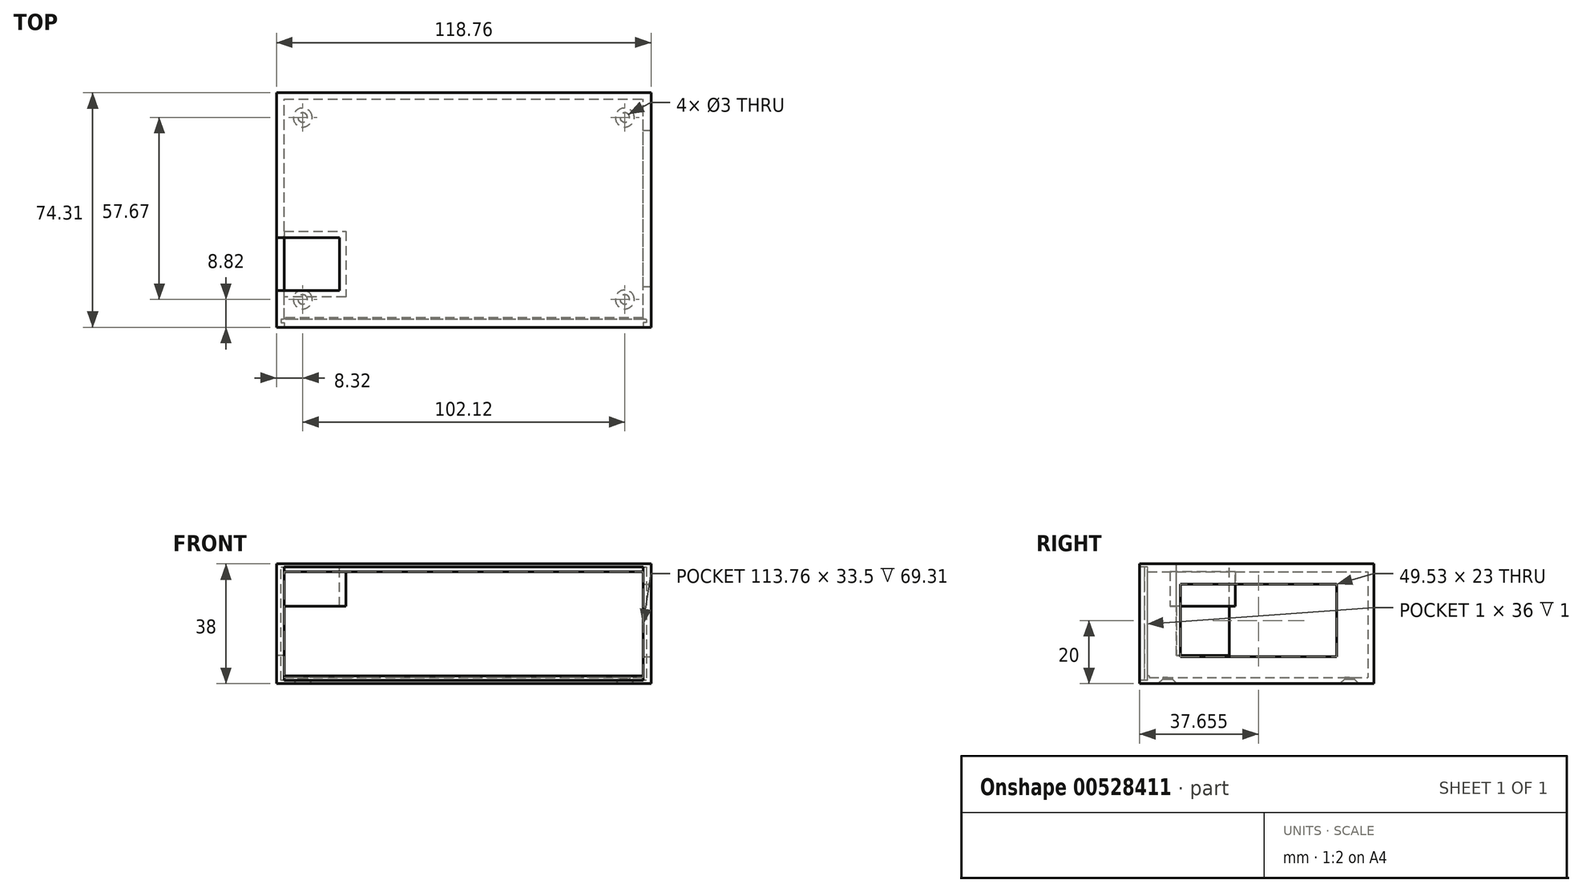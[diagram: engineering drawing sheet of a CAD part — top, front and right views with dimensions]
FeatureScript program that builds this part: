
annotation { "Feature Type Name" : "Feature", "Feature Type Description" : "" }
export const myFeature = defineFeature(function(context is Context, id is Id, definition is map)
    precondition{}
    {
        {
            var Q0;
            Q0=qCreatedBy(makeId("Top.planeOp"),FACE);
            var sketch = newSketch(context, id + "F0", { "sketchPlane" : qUnion([Q0])});
            skLineSegment(sketch, "E0.bottom", {"start": v(0, 0) * mm, "end": v(111.76, 0) * mm, "construction": true});
            skLineSegment(sketch, "E0.top", {"start": v(0, 67.31) * mm, "end": v(111.76, 67.31) * mm, "construction": true});
            skLineSegment(sketch, "E0.left", {"start": v(0, 0) * mm, "end": v(0, 67.3) * mm, "construction": true});
            skLineSegment(sketch, "E0.right", {"start": v(111.76, 0) * mm, "end": v(111.76, 67.3) * mm, "construction": true});
            skLineSegment(sketch, "E1", {"start": v(0, 4.82) * mm, "end": v(4.82, 4.82) * mm, "construction": true});
            skLineSegment(sketch, "E2", {"start": v(4.82, 4.82) * mm, "end": v(4.82, 0) * mm, "construction": true});
            skCircle(sketch, "E3", {"center": v(4.82, 4.82) * mm, "radius": 1.5 * mm});
            skLineSegment(sketch, "E4", {"start": v(0, 33.65) * mm, "end": v(111.76, 33.65) * mm, "construction": true});
            skLineSegment(sketch, "E5", {"start": v(55.88, 67.31) * mm, "end": v(55.88, 0) * mm, "construction": true});
            skCircle(sketch, "E6.MirrorC", {"center": v(4.82, 62.49) * mm, "radius": 1.5 * mm});
            skCircle(sketch, "E7.MirrorC", {"center": v(106.94, 62.5) * mm, "radius": 1.5 * mm});
            skCircle(sketch, "E8.MirrorC", {"center": v(106.94, 4.82) * mm, "radius": 1.5 * mm});
            skLineSegment(sketch, "E9.bottom", {"start": v(-1, -1) * mm, "end": v(112.76, -1) * mm});
            skLineSegment(sketch, "E9.top", {"start": v(-1, 68.31) * mm, "end": v(112.76, 68.31) * mm});
            skLineSegment(sketch, "E9.left", {"start": v(-1, -1) * mm, "end": v(-1, 68.31) * mm});
            skLineSegment(sketch, "E9.right", {"start": v(112.76, -1) * mm, "end": v(112.76, 68.31) * mm});
            skLineSegment(sketch, "E10", {"start": v(0, 0) * mm, "end": v(0, -1) * mm, "construction": true});
            skLineSegment(sketch, "E11", {"start": v(0, 0) * mm, "end": v(-1, 0) * mm, "construction": true});
            skLineSegment(sketch, "E12", {"start": v(0, 67.31) * mm, "end": v(0, 68.31) * mm, "construction": true});
            skLineSegment(sketch, "E13", {"start": v(111.76, 67.31) * mm, "end": v(112.76, 67.31) * mm, "construction": true});
            skLineSegment(sketch, "E14.bottom", {"start": v(-3.5, -4) * mm, "end": v(115.26, -4) * mm});
            skLineSegment(sketch, "E14.top", {"start": v(-3.5, 70.31) * mm, "end": v(115.26, 70.31) * mm});
            skLineSegment(sketch, "E14.left", {"start": v(-3.5, -4) * mm, "end": v(-3.5, 70.31) * mm});
            skLineSegment(sketch, "E14.right", {"start": v(115.26, -4) * mm, "end": v(115.26, 70.31) * mm});
            skLineSegment(sketch, "E15", {"start": v(-1, -1) * mm, "end": v(-1, -4) * mm, "construction": true});
            skLineSegment(sketch, "E16", {"start": v(-1, -1) * mm, "end": v(-3.5, -1) * mm, "construction": true});
            skLineSegment(sketch, "E17", {"start": v(-1, 68.31) * mm, "end": v(-1, 70.31) * mm, "construction": true});
            skLineSegment(sketch, "E18", {"start": v(112.76, 68.31) * mm, "end": v(115.26, 68.31) * mm, "construction": true});
            skCircle(sketch, "E19", {"center": v(4.82, 4.82) * mm, "radius": 3 * mm});
            skCircle(sketch, "E20.MirrorC", {"center": v(4.82, 62.49) * mm, "radius": 3 * mm});
            skCircle(sketch, "E21.MirrorC", {"center": v(106.94, 62.5) * mm, "radius": 3 * mm});
            skCircle(sketch, "E22.MirrorC", {"center": v(106.94, 4.82) * mm, "radius": 3 * mm});
            skSolve(sketch);
        }
        {
            var Q0;
            Q0=makeQuery(id+"F0.imprint","IMPRINT",FACE,{"disambiguationData":[TD([[makeQuery(id+"F0.imprint","IMPRINT",EDGE,{"derivedFrom":sQuery(id+"F0.wireOp",EDGE,"E9.bottom")}),1.0]])]});
            var Q1;
            Q1=makeQuery(id+"F0.imprint","IMPRINT",FACE,{"disambiguationData":[TD([[makeQuery(id+"F0.imprint","IMPRINT",EDGE,{"derivedFrom":sQuery(id+"F0.wireOp",EDGE,"E7.MirrorC")}),-1.0]])]});
            var Q2;
            Q2=makeQuery(id+"F0.imprint","IMPRINT",FACE,{"disambiguationData":[TD([[makeQuery(id+"F0.imprint","IMPRINT",EDGE,{"derivedFrom":sQuery(id+"F0.wireOp",EDGE,"E7.MirrorC")}),1.0]])]});
            var Q3;
            Q3=makeQuery(id+"F0.imprint","IMPRINT",FACE,{"disambiguationData":[TD([[makeQuery(id+"F0.imprint","IMPRINT",EDGE,{"derivedFrom":sQuery(id+"F0.wireOp",EDGE,"E8.MirrorC")}),1.0]])]});
            var Q4;
            Q4=makeQuery(id+"F0.imprint","IMPRINT",FACE,{"disambiguationData":[TD([[makeQuery(id+"F0.imprint","IMPRINT",EDGE,{"derivedFrom":sQuery(id+"F0.wireOp",EDGE,"E8.MirrorC")}),-1.0]])]});
            var Q5;
            Q5=makeQuery(id+"F0.imprint","IMPRINT",FACE,{"disambiguationData":[TD([[makeQuery(id+"F0.imprint","IMPRINT",EDGE,{"derivedFrom":sQuery(id+"F0.wireOp",EDGE,"E3")}),-1.0]])]});
            var Q6;
            Q6=makeQuery(id+"F0.imprint","IMPRINT",FACE,{"disambiguationData":[TD([[makeQuery(id+"F0.imprint","IMPRINT",EDGE,{"derivedFrom":sQuery(id+"F0.wireOp",EDGE,"E3")}),1.0]])]});
            var Q7;
            Q7=makeQuery(id+"F0.imprint","IMPRINT",FACE,{"disambiguationData":[TD([[makeQuery(id+"F0.imprint","IMPRINT",EDGE,{"derivedFrom":sQuery(id+"F0.wireOp",EDGE,"E6.MirrorC")}),1.0]])]});
            var Q8;
            Q8=makeQuery(id+"F0.imprint","IMPRINT",FACE,{"disambiguationData":[TD([[makeQuery(id+"F0.imprint","IMPRINT",EDGE,{"derivedFrom":sQuery(id+"F0.wireOp",EDGE,"E6.MirrorC")}),-1.0]])]});
            extrude(context, id + "F1", {"entities" : qUnion([Q0, Q1, Q2, Q3, Q4, Q5, Q6, Q7, Q8]), "depth" : 2 * mm, "offsetDistance" : 25 * mm});
        }
        {
            var Q0;
            Q0=makeQuery(id+"F0.imprint","IMPRINT",FACE,{"disambiguationData":[TD([[makeQuery(id+"F0.imprint","IMPRINT",EDGE,{"derivedFrom":sQuery(id+"F0.wireOp",EDGE,"E9.bottom")}),-1.0]])]});
            extrude(context, id + "F2", {"entities" : qUnion([Q0]), "operationType" : NewBodyOperationType.ADD, "depth" : 38 * mm, "offsetDistance" : 25 * mm});
        }
        {
            var Q0;
            Q0=makeQuery(id+"F2.opExtrude","SWEPT_FACE",FACE,{"disambiguationData":[OSD([sQuery(id+"F0.wireOp",EDGE,"E14.right")])]});
            var sketch = newSketch(context, id + "F3", { "sketchPlane" : qUnion([Q0])});
            skLineSegment(sketch, "E23.bottom", {"start": v(-4, 38) * mm, "end": v(70.31, 38) * mm});
            skLineSegment(sketch, "E23.top", {"start": v(-4, 0) * mm, "end": v(70.31, 0) * mm});
            skLineSegment(sketch, "E23.left", {"start": v(-4, 38) * mm, "end": v(-4, 0) * mm});
            skLineSegment(sketch, "E23.right", {"start": v(70.31, 38) * mm, "end": v(70.31, 0) * mm});
            skLineSegment(sketch, "E24", {"start": v(0, 0) * mm, "end": v(0, 2.5) * mm, "construction": true});
            skLineSegment(sketch, "E25", {"start": v(0, 2.5) * mm, "end": v(0, 8.5) * mm, "construction": true});
            skLineSegment(sketch, "E26", {"start": v(0, 8.5) * mm, "end": v(8.89, 8.5) * mm, "construction": true});
            skLineSegment(sketch, "E27", {"start": v(0, 8.5) * mm, "end": v(-4, 8.5) * mm, "construction": true});
            skLineSegment(sketch, "E28", {"start": v(8.9, 8.5) * mm, "end": v(8.9, 31.5) * mm});
            skLineSegment(sketch, "E29", {"start": v(8.89, 8.5) * mm, "end": v(58.42, 8.5) * mm});
            skLineSegment(sketch, "E30", {"start": v(58.42, 8.5) * mm, "end": v(67.3, 8.5) * mm, "construction": true});
            skLineSegment(sketch, "E31", {"start": v(67.3, 8.5) * mm, "end": v(70.31, 8.5) * mm, "construction": true});
            skLineSegment(sketch, "E32", {"start": v(8.89, 31.5) * mm, "end": v(58.42, 31.5) * mm});
            skLineSegment(sketch, "E33", {"start": v(58.42, 31.5) * mm, "end": v(58.42, 8.5) * mm});
            skSolve(sketch);
        }
        {
            var Q0;
            Q0=makeQuery(id+"F3.imprint","IMPRINT",FACE,{"disambiguationData":[TD([[makeQuery(id+"F3.imprint","IMPRINT",EDGE,{"derivedFrom":sQuery(id+"F3.wireOp",EDGE,"E28")}),-1.0]])]});
            extrude(context, id + "F4", {"entities" : qUnion([Q0]), "operationType" : NewBodyOperationType.REMOVE, "endBound" : BoundingType.UP_TO_NEXT, "oppositeDirection" : true, "depth" : 25 * mm, "offsetDistance" : 25 * mm});
        }
        {
            var Q0;
            Q0=makeQuery(id+"F2.opExtrude","SWEPT_FACE",FACE,{"disambiguationData":[OSD([sQuery(id+"F0.wireOp",EDGE,"E14.left")])]});
            var sketch = newSketch(context, id + "F5", { "sketchPlane" : qUnion([Q0])});
            skLineSegment(sketch, "E34", {"start": v(0, 0) * mm, "end": v(0, 9) * mm, "construction": true});
            skLineSegment(sketch, "E35", {"start": v(0, 9) * mm, "end": v(-7.62, 9) * mm, "construction": true});
            skLineSegment(sketch, "E36", {"start": v(-7.62, 9) * mm, "end": v(-24.38, 9) * mm});
            skLineSegment(sketch, "E37", {"start": v(-24.38, 9) * mm, "end": v(-24.38, 38) * mm});
            skLineSegment(sketch, "E38.bottom", {"start": v(-70.31, 38) * mm, "end": v(4, 38) * mm});
            skLineSegment(sketch, "E38.top", {"start": v(-70.31, 0) * mm, "end": v(4, 0) * mm});
            skLineSegment(sketch, "E38.left", {"start": v(-70.31, 38) * mm, "end": v(-70.31, 0) * mm});
            skLineSegment(sketch, "E38.right", {"start": v(4, 38) * mm, "end": v(4, 0) * mm});
            skLineSegment(sketch, "E39", {"start": v(-7.62, 9) * mm, "end": v(-7.62, 38) * mm});
            skSolve(sketch);
        }
        {
            var Q0;
            Q0=makeQuery(id+"F5.imprint","IMPRINT",FACE,{"disambiguationData":[TD([[makeQuery(id+"F5.imprint","IMPRINT",EDGE,{"derivedFrom":sQuery(id+"F5.wireOp",EDGE,"E36")}),-1.0]])]});
            extrude(context, id + "F6", {"entities" : qUnion([Q0]), "operationType" : NewBodyOperationType.REMOVE, "endBound" : BoundingType.UP_TO_NEXT, "oppositeDirection" : true, "depth" : 25 * mm, "offsetDistance" : 25 * mm});
        }
        {
            var Q0;
            Q0=makeQuery(id+"F2.opExtrude","CAP_FACE",FACE,{"disambiguationData":[OSD([sQuery(id+"F0.wireOp",EDGE,"E9.bottom"),sQuery(id+"F0.wireOp",EDGE,"E9.top"),sQuery(id+"F0.wireOp",EDGE,"E9.left"),sQuery(id+"F0.wireOp",EDGE,"E9.right"),sQuery(id+"F0.wireOp",EDGE,"E14.bottom"),sQuery(id+"F0.wireOp",EDGE,"E14.top"),sQuery(id+"F0.wireOp",EDGE,"E14.left"),sQuery(id+"F0.wireOp",EDGE,"E14.right")])],"isStart":false});
            var sketch = newSketch(context, id + "F7", { "sketchPlane" : qUnion([Q0])});
            skLineSegment(sketch, "E40.bottom", {"start": v(-1, -1) * mm, "end": v(112.76, -1) * mm});
            skLineSegment(sketch, "E40.top", {"start": v(-1, 68.31) * mm, "end": v(112.76, 68.31) * mm});
            skLineSegment(sketch, "E40.left", {"start": v(-1, -1) * mm, "end": v(-1, 68.31) * mm});
            skLineSegment(sketch, "E40.right", {"start": v(112.76, -1) * mm, "end": v(112.76, 68.31) * mm});
            skLineSegment(sketch, "E41", {"start": v(-1, 24.38) * mm, "end": v(18.5, 24.38) * mm});
            skLineSegment(sketch, "E42", {"start": v(18.5, 24.38) * mm, "end": v(18.5, 7.62) * mm});
            skLineSegment(sketch, "E43", {"start": v(18.5, 7.62) * mm, "end": v(-1, 7.62) * mm});
            skSolve(sketch);
        }
        {
            var Q0;
            {var subQ4=sQuery(id+"F7.wireOp",EDGE,"E40.bottom");Q0=makeQuery(id+"F7.imprint","IMPRINT",FACE,{"disambiguationData":[TD([[makeQuery(id+"F7.imprint","IMPRINT",EDGE,{"derivedFrom":subQ4}),1.0]])]});}
            extrude(context, id + "F8", {"entities" : qUnion([Q0]), "operationType" : NewBodyOperationType.ADD, "oppositeDirection" : true, "depth" : 2.5 * mm, "offsetDistance" : 25 * mm});
        }
        {
            var Q0;
            Q0=makeQuery(id+"F8.boolean.opBoolean","MERGE",FACE,{"derivedFrom":[makeQuery(id+"F6.boolean.opBoolean","COPY",FACE,{"derivedFrom":makeQuery(id+"F6.opExtrude","SWEPT_FACE",FACE,{"disambiguationData":[OSD([sQuery(id+"F5.wireOp",EDGE,"E37")])]})}),makeQuery(id+"F8.opExtrude","SWEPT_FACE",FACE,{"disambiguationData":[OSD([sQuery(id+"F7.wireOp",EDGE,"E41")])]})]});
            var sketch = newSketch(context, id + "F9", { "sketchPlane" : qUnion([Q0])});
            skLineSegment(sketch, "E44", {"start": v(18.5, 35.5) * mm, "end": v(-1, 35.5) * mm});
            skLineSegment(sketch, "E45", {"start": v(-1, 35.5) * mm, "end": v(-1, 24.5) * mm});
            skLineSegment(sketch, "E46", {"start": v(-1, 24.5) * mm, "end": v(18.5, 24.5) * mm});
            skLineSegment(sketch, "E47", {"start": v(18.5, 24.5) * mm, "end": v(18.5, 35.5) * mm});
            skSolve(sketch);
        }
        {
            var Q0;
            Q0=makeQuery(id+"F9.imprint","IMPRINT",FACE,{"disambiguationData":[TD([[makeQuery(id+"F9.imprint","IMPRINT",EDGE,{"derivedFrom":sQuery(id+"F9.wireOp",EDGE,"E44")}),-1.0]])]});
            extrude(context, id + "F10", {"entities" : qUnion([Q0]), "operationType" : NewBodyOperationType.ADD, "oppositeDirection" : true, "depth" : 2 * mm, "offsetDistance" : 25 * mm});
        }
        {
            var Q0;
            Q0=makeQuery(id+"F8.boolean.opBoolean","MERGE",FACE,{"derivedFrom":[makeQuery(id+"F6.boolean.opBoolean","COPY",FACE,{"derivedFrom":makeQuery(id+"F6.opExtrude","SWEPT_FACE",FACE,{"disambiguationData":[OSD([sQuery(id+"F5.wireOp",EDGE,"E39")])]})}),makeQuery(id+"F8.opExtrude","SWEPT_FACE",FACE,{"disambiguationData":[OSD([sQuery(id+"F7.wireOp",EDGE,"E43")])]})]});
            var sketch = newSketch(context, id + "F11", { "sketchPlane" : qUnion([Q0])});
            skLineSegment(sketch, "E48", {"start": v(-18.5, 35.5) * mm, "end": v(-18.5, 24.5) * mm});
            skLineSegment(sketch, "E49", {"start": v(-18.5, 24.5) * mm, "end": v(1, 24.5) * mm});
            skLineSegment(sketch, "E50", {"start": v(1, 24.5) * mm, "end": v(1, 35.5) * mm});
            skLineSegment(sketch, "E51", {"start": v(1, 35.5) * mm, "end": v(-18.5, 35.5) * mm});
            skSolve(sketch);
        }
        {
            var Q0;
            Q0=makeQuery(id+"F11.imprint","IMPRINT",FACE,{"disambiguationData":[TD([[makeQuery(id+"F11.imprint","IMPRINT",EDGE,{"derivedFrom":sQuery(id+"F11.wireOp",EDGE,"E48")}),1.0]])]});
            extrude(context, id + "F12", {"entities" : qUnion([Q0]), "operationType" : NewBodyOperationType.ADD, "oppositeDirection" : true, "depth" : 2 * mm, "offsetDistance" : 25 * mm});
        }
        {
            var Q0;
            Q0=makeQuery(id+"F8.opExtrude","SWEPT_FACE",FACE,{"disambiguationData":[OSD([sQuery(id+"F7.wireOp",EDGE,"E42")])]});
            var sketch = newSketch(context, id + "F13", { "sketchPlane" : qUnion([Q0])});
            skLineSegment(sketch, "E52.bottom", {"start": v(-24.38, 38) * mm, "end": v(-7.62, 38) * mm});
            skLineSegment(sketch, "E52.top", {"start": v(-24.38, 24.5) * mm, "end": v(-7.62, 24.5) * mm});
            skLineSegment(sketch, "E52.left", {"start": v(-24.38, 38) * mm, "end": v(-24.38, 24.5) * mm});
            skLineSegment(sketch, "E52.right", {"start": v(-7.62, 38) * mm, "end": v(-7.62, 24.5) * mm});
            skSolve(sketch);
        }
        {
            var Q0;
            Q0 = qSketchRegion(id + "F13", true);
            extrude(context, id + "F14", {"entities" : qUnion([Q0]), "operationType" : NewBodyOperationType.ADD, "depth" : 2 * mm, "offsetDistance" : 25 * mm});
        }
        {
            var Q0;
            Q0=makeQuery(id+"F2.opExtrude","SWEPT_FACE",FACE,{"disambiguationData":[OSD([sQuery(id+"F0.wireOp",EDGE,"E14.bottom")])]});
            var sketch = newSketch(context, id + "F15", { "sketchPlane" : qUnion([Q0])});
            skLineSegment(sketch, "E53.bottom", {"start": v(-3.5, 0) * mm, "end": v(115.26, 0) * mm});
            skLineSegment(sketch, "E53.top", {"start": v(-3.5, 38) * mm, "end": v(115.26, 38) * mm});
            skLineSegment(sketch, "E53.left", {"start": v(-3.5, 0) * mm, "end": v(-3.5, 38) * mm});
            skLineSegment(sketch, "E53.right", {"start": v(115.26, 0) * mm, "end": v(115.26, 38) * mm});
            skLineSegment(sketch, "E54", {"start": v(-1, 37) * mm, "end": v(-1, 38) * mm, "construction": true});
            skLineSegment(sketch, "E55", {"start": v(-1, 37) * mm, "end": v(-3.5, 37) * mm, "construction": true});
            skLineSegment(sketch, "E56", {"start": v(115.26, 1) * mm, "end": v(112.76, 1) * mm, "construction": true});
            skLineSegment(sketch, "E57", {"start": v(112.76, 1) * mm, "end": v(112.76, 0) * mm, "construction": true});
            skLineSegment(sketch, "E58.bottom", {"start": v(-1, 37) * mm, "end": v(112.76, 37) * mm});
            skLineSegment(sketch, "E58.top", {"start": v(-1, 1) * mm, "end": v(112.76, 1) * mm});
            skLineSegment(sketch, "E58.left", {"start": v(-1, 37) * mm, "end": v(-1, 1) * mm});
            skLineSegment(sketch, "E58.right", {"start": v(112.76, 37) * mm, "end": v(112.76, 1) * mm});
            skLineSegment(sketch, "E59", {"start": v(112.76, 2.5) * mm, "end": v(-1, 2.5) * mm});
            skLineSegment(sketch, "E60", {"start": v(112.76, 35.5) * mm, "end": v(-1, 35.5) * mm});
            skSolve(sketch);
        }
        {
            var Q0;
            {var subQ0=sQuery(id+"F15.wireOp",EDGE,"E59");Q0=makeQuery(id+"F15.imprint","IMPRINT",FACE,{"disambiguationData":[TD([[makeQuery(id+"F15.imprint","IMPRINT",EDGE,{"derivedFrom":subQ0}),-1.0]])]});}
            extrude(context, id + "F16", {"entities" : qUnion([Q0]), "operationType" : NewBodyOperationType.REMOVE, "endBound" : BoundingType.UP_TO_NEXT, "oppositeDirection" : true, "depth" : 25 * mm, "offsetDistance" : 25 * mm});
        }
        {
            var Q0;
            Q0=makeQuery(id+"F2.opExtrude","SWEPT_FACE",FACE,{"disambiguationData":[OSD([sQuery(id+"F0.wireOp",EDGE,"E14.bottom")])]});
            var sketch = newSketch(context, id + "F17", { "sketchPlane" : qUnion([Q0])});
            skLineSegment(sketch, "E61.bottom", {"start": v(-1, 35.5) * mm, "end": v(112.76, 35.5) * mm});
            skLineSegment(sketch, "E61.top", {"start": v(-1, 2.5) * mm, "end": v(112.76, 2.5) * mm});
            skLineSegment(sketch, "E61.left", {"start": v(-1, 35.5) * mm, "end": v(-1, 2.5) * mm});
            skLineSegment(sketch, "E61.right", {"start": v(112.76, 35.5) * mm, "end": v(112.76, 2.5) * mm});
            skLineSegment(sketch, "E62", {"start": v(112.76, 2.5) * mm, "end": v(112.76, 1) * mm});
            skLineSegment(sketch, "E63", {"start": v(112.76, 1) * mm, "end": v(-1, 1) * mm});
            skLineSegment(sketch, "E64", {"start": v(-1, 1) * mm, "end": v(-1, 2.5) * mm});
            skLineSegment(sketch, "E65", {"start": v(-1, 35.5) * mm, "end": v(-1, 37) * mm});
            skLineSegment(sketch, "E66", {"start": v(-1, 37) * mm, "end": v(112.76, 37) * mm});
            skLineSegment(sketch, "E67", {"start": v(112.76, 37) * mm, "end": v(112.76, 35.5) * mm});
            skSolve(sketch);
        }
        {
            var Q0;
            Q0=makeQuery(id+"F17.imprint","IMPRINT",FACE,{"disambiguationData":[TD([[makeQuery(id+"F17.imprint","IMPRINT",EDGE,{"derivedFrom":sQuery(id+"F17.wireOp",EDGE,"E61.bottom")}),-1.0]])]});
            var Q1;
            Q1=makeQuery(id+"F17.imprint","IMPRINT",FACE,{"disambiguationData":[TD([[makeQuery(id+"F17.imprint","IMPRINT",EDGE,{"derivedFrom":sQuery(id+"F17.wireOp",EDGE,"E61.top")}),1.0]])]});
            extrude(context, id + "F18", {"entities" : qUnion([Q0, Q1]), "operationType" : NewBodyOperationType.REMOVE, "oppositeDirection" : true, "depth" : 2.5 * mm, "offsetDistance" : 25 * mm});
        }
        {
            var Q0;
            Q0=makeQuery(id+"F18.boolean.opBoolean","MERGE",FACE,{"derivedFrom":[makeQuery(id+"F16.boolean.opBoolean","MERGE",FACE,{"derivedFrom":[makeQuery(id+"F2.opExtrude","SWEPT_FACE",FACE,{"disambiguationData":[OSD([sQuery(id+"F0.wireOp",EDGE,"E9.left")])]}),makeQuery(id+"F16.opExtrude","SWEPT_FACE",FACE,{"disambiguationData":[OSD([sQuery(id+"F15.wireOp",EDGE,"E58.left")])]})]}),makeQuery(id+"F18.opExtrude","SWEPT_FACE",FACE,{"disambiguationData":[OSD([sQuery(id+"F17.wireOp",EDGE,"E64")])]}),makeQuery(id+"F18.opExtrude","SWEPT_FACE",FACE,{"disambiguationData":[OSD([sQuery(id+"F17.wireOp",EDGE,"E65")])]})]});
            var sketch = newSketch(context, id + "F19", { "sketchPlane" : qUnion([Q0])});
            skLineSegment(sketch, "E68", {"start": v(-1.5, 37) * mm, "end": v(-2.5, 37) * mm});
            skLineSegment(sketch, "E69", {"start": v(-1.5, 1) * mm, "end": v(-1.5, 37) * mm});
            skLineSegment(sketch, "E70", {"start": v(-1.5, 1) * mm, "end": v(-2.5, 1) * mm});
            skLineSegment(sketch, "E71", {"start": v(-2.5, 1) * mm, "end": v(-2.5, 37) * mm});
            skSolve(sketch);
        }
        {
            var Q0;
            {var subQ4=sQuery(id+"F19.wireOp",EDGE,"E68");Q0=makeQuery(id+"F19.imprint","IMPRINT",FACE,{"disambiguationData":[TD([[makeQuery(id+"F19.imprint","IMPRINT",EDGE,{"derivedFrom":subQ4}),1.0]])]});}
            extrude(context, id + "F20", {"entities" : qUnion([Q0]), "operationType" : NewBodyOperationType.REMOVE, "oppositeDirection" : true, "depth" : 1 * mm, "offsetDistance" : 25 * mm});
        }
        {
            var Q0;
            Q0=makeQuery(id+"F18.boolean.opBoolean","MERGE",FACE,{"derivedFrom":[makeQuery(id+"F16.boolean.opBoolean","MERGE",FACE,{"derivedFrom":[makeQuery(id+"F2.opExtrude","SWEPT_FACE",FACE,{"disambiguationData":[OSD([sQuery(id+"F0.wireOp",EDGE,"E9.right")])]}),makeQuery(id+"F16.opExtrude","SWEPT_FACE",FACE,{"disambiguationData":[OSD([sQuery(id+"F15.wireOp",EDGE,"E58.right")])]})]}),makeQuery(id+"F18.opExtrude","SWEPT_FACE",FACE,{"disambiguationData":[OSD([sQuery(id+"F17.wireOp",EDGE,"E62")])]}),makeQuery(id+"F18.opExtrude","SWEPT_FACE",FACE,{"disambiguationData":[OSD([sQuery(id+"F17.wireOp",EDGE,"E67")])]})]});
            var sketch = newSketch(context, id + "F21", { "sketchPlane" : qUnion([Q0])});
            skLineSegment(sketch, "E72", {"start": v(1.5, 37) * mm, "end": v(1.5, 1) * mm});
            skLineSegment(sketch, "E73", {"start": v(1.5, 1) * mm, "end": v(2.5, 1) * mm});
            skLineSegment(sketch, "E74", {"start": v(1.5, 37) * mm, "end": v(2.5, 37) * mm});
            skLineSegment(sketch, "E75", {"start": v(2.5, 37) * mm, "end": v(2.5, 1) * mm});
            skSolve(sketch);
        }
        {
            var Q0;
            {var subQ0=sQuery(id+"F21.wireOp",EDGE,"E73");Q0=makeQuery(id+"F21.imprint","IMPRINT",FACE,{"disambiguationData":[TD([[makeQuery(id+"F21.imprint","IMPRINT",EDGE,{"derivedFrom":subQ0}),1.0]])]});}
            extrude(context, id + "F22", {"entities" : qUnion([Q0]), "operationType" : NewBodyOperationType.REMOVE, "oppositeDirection" : true, "depth" : 1 * mm, "offsetDistance" : 25 * mm});
        }
        {
            var Q0;
            Q0=sQuery(id+"F0.wireOp",VERTEX,"E2.start");
            var Q1;
            Q1=sQuery(id+"F0.wireOp",VERTEX,"E8.MirrorC.center");
            var Q2;
            Q2=sQuery(id+"F0.wireOp",VERTEX,"E7.MirrorC.center");
            var Q3;
            Q3=sQuery(id+"F0.wireOp",VERTEX,"E6.MirrorC.center");
            var Q4;
            Q4=makeQuery(id+"F1.opExtrude","SWEPT_BODY",BODY,{"disambiguationData":[OSD([sQuery(id+"F0.wireOp",EDGE,"E9.bottom"),sQuery(id+"F0.wireOp",EDGE,"E9.top"),sQuery(id+"F0.wireOp",EDGE,"E9.left"),sQuery(id+"F0.wireOp",EDGE,"E9.right")])]});
            hole(context, id + "F23", {"style" : HoleStyle.C_SINK, "endStyle" : HoleEndStyle.BLIND, "oppositeDirection" : true, "holeDiameter" : 3 * mm, "cSinkDiameter" : 6 * mm, "cSinkAngle" : 90 * degree, "holeDepth" : 5 * mm, "isTappedThrough" : true, "tappedDepth" : 12 * mm, "tapClearance" : 3, "locations" : qUnion([Q0, Q1, Q2, Q3]), "scope" : qUnion([Q4])});
        }
    });
